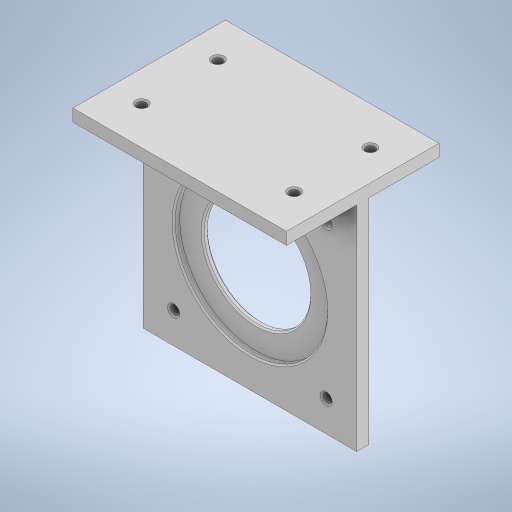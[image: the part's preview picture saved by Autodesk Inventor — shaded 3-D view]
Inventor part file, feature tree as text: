
AUTODESK INVENTOR PART (.ipt)
format: ipt  version: 2023 (Build 270158000, 158)  size: 329,728 bytes
history: native  units: mm
features: extrude x3, sketch x3, other x1, chamfer x1
ambient origin geometry x8: Origin, YZ Plane, XZ Plane, XY Plane, X Axis, Y Axis, Z Axis, Center Point
bodies: Body1 (feature_tree)
feature tree (8):
  other  "Твердое тело1"
  extrude  "Выдавливание1"  Depth=140.0mm
  extrude  "Выдавливание2"  Depth=140.0mm
  extrude  "Выдавливание3"  Depth=100.0mm
  chamfer  "Фаска1"  Distance=20.0mm
  sketch  "Эскиз1"
  sketch  "Эскиз2"
  sketch  "Эскиз3"
